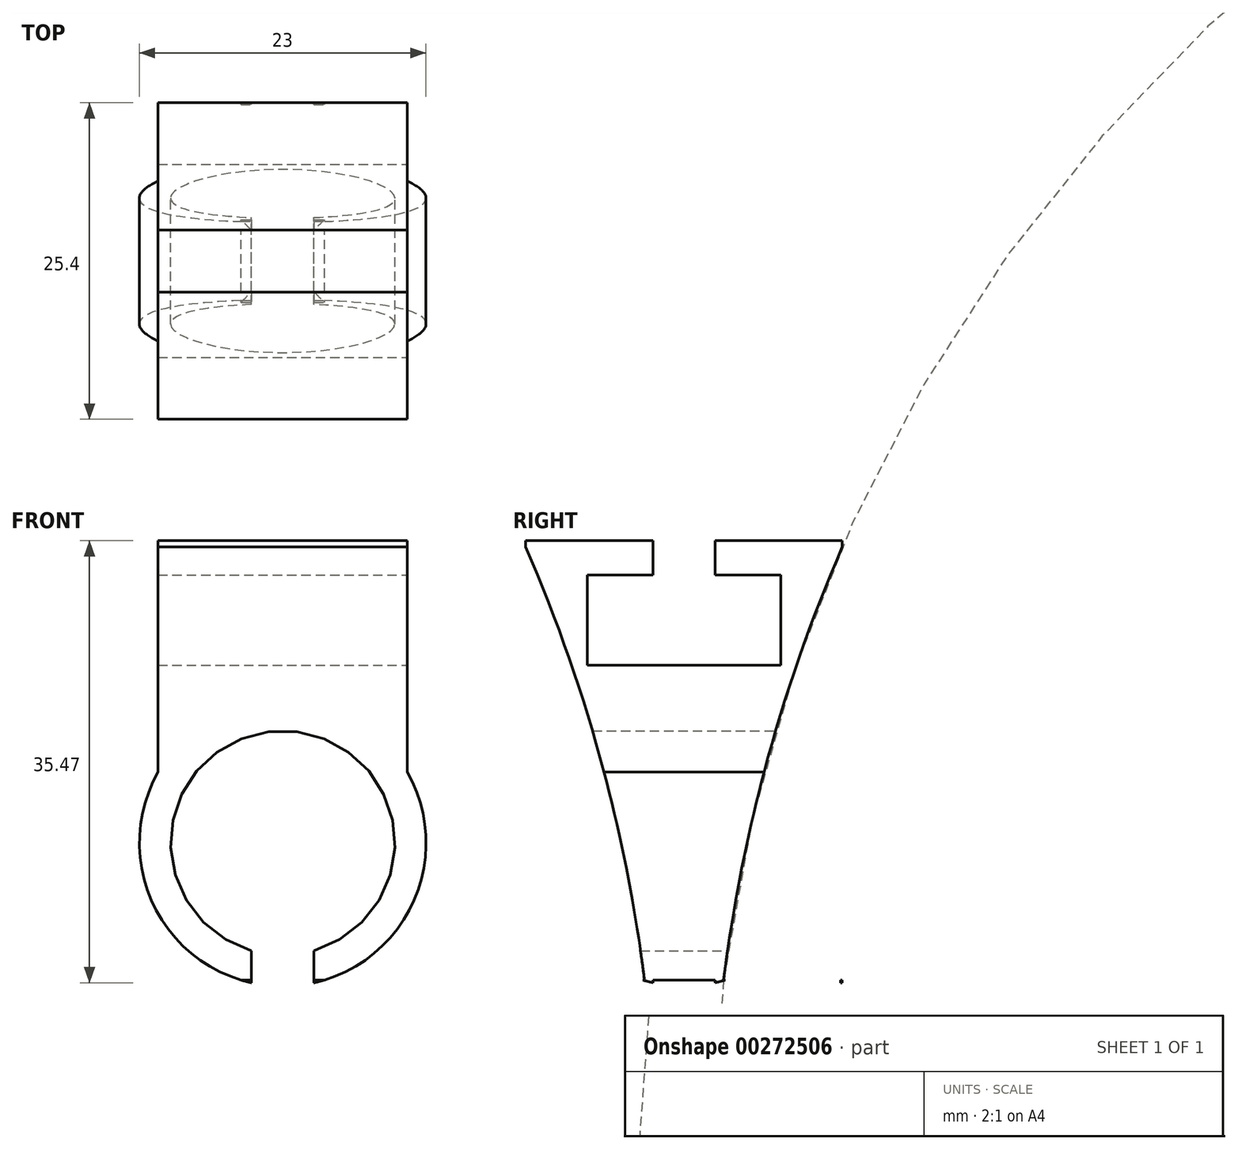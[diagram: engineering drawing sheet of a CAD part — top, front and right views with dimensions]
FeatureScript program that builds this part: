
annotation { "Feature Type Name" : "Feature", "Feature Type Description" : "" }
export const myFeature = defineFeature(function(context is Context, id is Id, definition is map)
    precondition{}
    {
        {
            var Q0;
            Q0=qCreatedBy(makeId("Front.planeOp"),FACE);
            var sketch = newSketch(context, id + "F0", { "sketchPlane" : qUnion([Q0])});
            skArc(sketch, "E0", {"start": v(2.5, -8.65) * mm, "mid": v(0, 9) * mm, "end": v(-2.5, -8.65) * mm});
            skArc(sketch, "E1", {"start": v(2.5, -11.22) * mm, "mid": v(0, 11.5) * mm, "end": v(-2.5, -11.22) * mm});
            skLineSegment(sketch, "E2.left", {"start": v(-2.5, -11.22) * mm, "end": v(-2.5, -8.65) * mm});
            skLineSegment(sketch, "E2.right", {"start": v(2.5, -11.22) * mm, "end": v(2.5, -8.65) * mm});
            skLineSegment(sketch, "E3.bottom", {"start": v(-10, 24.25) * mm, "end": v(-2.5, 24.25) * mm});
            skLineSegment(sketch, "E3.left", {"start": v(-10, 24.25) * mm, "end": v(-10, 11.5) * mm});
            skLineSegment(sketch, "E3.right", {"start": v(10, 24.25) * mm, "end": v(10, 11.5) * mm});
            skLineSegment(sketch, "E4", {"start": v(-2.5, 24.25) * mm, "end": v(-10, 24.25) * mm});
            skLineSegment(sketch, "E5", {"start": v(10, 24.25) * mm, "end": v(2.5, 24.25) * mm});
            skLineSegment(sketch, "E6", {"start": v(2.5, 24.25) * mm, "end": v(10, 24.25) * mm});
            skPoint(sketch, "E7", {"position": v(0, 11.5) * mm});
            skLineSegment(sketch, "E8", {"start": v(-10, 11.5) * mm, "end": v(-10, 5.68) * mm});
            skLineSegment(sketch, "E9", {"start": v(10, 11.5) * mm, "end": v(10, 5.68) * mm});
            skPoint(sketch, "E10.orphan", {"position": v(2.5, 11.5) * mm});
            skPoint(sketch, "E11.end.orphan", {"position": v(-2.5, 11.5) * mm});
            skLineSegment(sketch, "E12", {"start": v(10, 24.25) * mm, "end": v(-10, 24.25) * mm});
            skSolve(sketch);
        }
        {
            var Q0;
            Q0 = qSketchRegion(id + "F0", true);
            extrude(context, id + "F1", {"entities" : qUnion([Q0]), "endBound" : BoundingType.SYMMETRIC, "depth" : 25.4 * mm, "offsetDistance" : 25.4 * mm});
        }
        {
            var Q0;
            Q0=qCreatedBy(makeId("Right.planeOp"),FACE);
            var sketch = newSketch(context, id + "F2", { "sketchPlane" : qUnion([Q0])});
            skLineSegment(sketch, "E13.bottom", {"start": v(12.7, 11) * mm, "end": v(-12.7, 11) * mm});
            skLineSegment(sketch, "E13.top", {"start": v(12.7, -11) * mm, "end": v(-12.7, -11) * mm});
            skLineSegment(sketch, "E13.left", {"start": v(12.7, 11) * mm, "end": v(12.7, -11) * mm});
            skLineSegment(sketch, "E13.right", {"start": v(-12.7, 11) * mm, "end": v(-12.7, -11) * mm});
            skPoint(sketch, "E13.middle", {"position": v(0, 0) * mm});
            skLineSegment(sketch, "E14.bottom", {"start": v(-12.7, -11) * mm, "end": v(12.7, -11) * mm});
            skLineSegment(sketch, "E14.top", {"start": v(-12.7, 23.75) * mm, "end": v(12.7, 23.75) * mm});
            skLineSegment(sketch, "E14.left", {"start": v(-12.7, -11) * mm, "end": v(-12.7, 23.75) * mm});
            skLineSegment(sketch, "E14.right", {"start": v(12.7, -11) * mm, "end": v(12.7, 23.75) * mm});
            skLineSegment(sketch, "E15", {"start": v(0, 0) * mm, "end": v(0, -11) * mm});
            skLineSegment(sketch, "E16", {"start": v(0, -11) * mm, "end": v(3.18, -11) * mm});
            skLineSegment(sketch, "E17", {"start": v(3.18, -11) * mm, "end": v(-3.18, -11) * mm});
            skLineSegment(sketch, "E18", {"start": v(-3.18, -11) * mm, "end": v(3.18, -11) * mm});
            skArc(sketch, "E19", {"start": v(-3.18, -11) * mm, "mid": v(-6.7, 6.71) * mm, "end": v(-12.7, 23.75) * mm});
            skArc(sketch, "E20", {"start": v(12.7, 23.75) * mm, "mid": v(6.7, 6.71) * mm, "end": v(3.17, -11) * mm});
            skLineSegment(sketch, "E21.bottom", {"start": v(-12.7, -11) * mm, "end": v(12.57, -11) * mm});
            skLineSegment(sketch, "E21.top", {"start": v(-12.7, -24.25) * mm, "end": v(12.57, -24.25) * mm});
            skLineSegment(sketch, "E21.left", {"start": v(-12.7, -11) * mm, "end": v(-12.7, -24.25) * mm});
            skLineSegment(sketch, "E21.right", {"start": v(12.57, -11) * mm, "end": v(12.57, -24.25) * mm});
            skArc(sketch, "E22", {"start": v(2.5, -8.64) * mm, "mid": v(0, 9) * mm, "end": v(-2.5, -8.64) * mm});
            skArc(sketch, "E23", {"start": v(2.5, -11.22) * mm, "mid": v(0, 11.5) * mm, "end": v(-2.5, -11.22) * mm});
            skLineSegment(sketch, "E24.left", {"start": v(-2.5, -11.22) * mm, "end": v(-2.5, -8.64) * mm});
            skLineSegment(sketch, "E24.right", {"start": v(2.5, -11.22) * mm, "end": v(2.5, -8.64) * mm});
            skLineSegment(sketch, "E25.bottom", {"start": v(-7.75, 21.5) * mm, "end": v(-2.5, 21.5) * mm});
            skLineSegment(sketch, "E25.top", {"start": v(-7.75, 14.26) * mm, "end": v(7.75, 14.26) * mm});
            skLineSegment(sketch, "E25.left", {"start": v(-7.75, 21.5) * mm, "end": v(-7.75, 14.26) * mm});
            skLineSegment(sketch, "E25.right", {"start": v(7.75, 21.5) * mm, "end": v(7.75, 14.26) * mm});
            skLineSegment(sketch, "E26.bottom", {"start": v(-10, 24.26) * mm, "end": v(-2.5, 24.26) * mm});
            skLineSegment(sketch, "E26.left", {"start": v(-10, 24.26) * mm, "end": v(-10, 11.5) * mm});
            skLineSegment(sketch, "E26.right", {"start": v(10, 24.26) * mm, "end": v(10, 11.5) * mm});
            skLineSegment(sketch, "E27", {"start": v(-2.5, 24.26) * mm, "end": v(-10, 24.26) * mm});
            skLineSegment(sketch, "E28", {"start": v(10, 24.26) * mm, "end": v(2.5, 24.26) * mm});
            skLineSegment(sketch, "E29", {"start": v(2.5, 24.26) * mm, "end": v(10, 24.26) * mm});
            skLineSegment(sketch, "E30", {"start": v(-2.5, 24.26) * mm, "end": v(-2.5, 21.5) * mm});
            skLineSegment(sketch, "E31", {"start": v(-2.5, 21.5) * mm, "end": v(-2.5, 24.26) * mm});
            skLineSegment(sketch, "E32", {"start": v(2.5, 24.26) * mm, "end": v(2.5, 21.5) * mm});
            skPoint(sketch, "E33", {"position": v(0, 11.5) * mm});
            skLineSegment(sketch, "E34", {"start": v(-10, 11.5) * mm, "end": v(-10, 5.69) * mm});
            skLineSegment(sketch, "E35", {"start": v(10, 11.5) * mm, "end": v(10, 5.69) * mm});
            skLineSegment(sketch, "E36.trimOffspring", {"start": v(2.5, 21.5) * mm, "end": v(7.75, 21.5) * mm});
            skPoint(sketch, "E37.orphan", {"position": v(2.5, 11.5) * mm});
            skPoint(sketch, "E38.end.orphan", {"position": v(-2.5, 11.5) * mm});
            skLineSegment(sketch, "E39", {"start": v(2.5, 24.26) * mm, "end": v(-2.5, 24.26) * mm});
            skSolve(sketch);
        }
        {
            var Q0;
            {var subQ7=sQuery(id+"F2.wireOp",EDGE,"E14.left");Q0=makeQuery(id+"F2.imprint","IMPRINT",FACE,{"disambiguationData":[TD([[makeQuery(id+"F2.imprint","IMPRINT",EDGE,{"derivedFrom":subQ7}),-1.0]])]});}
            var Q1;
            {var subQ5=sQuery(id+"F2.wireOp",EDGE,"E39");Q1=makeQuery(id+"F2.imprint","IMPRINT",FACE,{"disambiguationData":[TD([[makeQuery(id+"F2.imprint","IMPRINT",EDGE,{"derivedFrom":subQ5}),1.0]])]});}
            var Q2;
            {var subQ5=sQuery(id+"F2.wireOp",EDGE,"E14.right");Q2=makeQuery(id+"F2.imprint","IMPRINT",FACE,{"disambiguationData":[TD([[makeQuery(id+"F2.imprint","IMPRINT",EDGE,{"derivedFrom":subQ5}),1.0]])]});}
            var Q3;
            {var subQ0=sQuery(id+"F2.wireOp",EDGE,"E35");var subQ1=sQuery(id+"F2.wireOp",EDGE,"E13.bottom");var subQ2=makeQuery(id+"F2.imprint","INTERSECT",VERTEX,{"derivedFrom":[subQ1,subQ0]});Q3=makeQuery(id+"F2.imprint","IMPRINT",FACE,{"disambiguationData":[TD([[makeQuery(id+"F2.imprint","IMPRINT",EDGE,{"disambiguationData":[TD([[subQ2,-1.0]])],"derivedFrom":subQ1}),-1.0]])]});}
            var Q4;
            {var subQ0=sQuery(id+"F2.wireOp",EDGE,"E34");var subQ1=sQuery(id+"F2.wireOp",EDGE,"E13.bottom");var subQ2=makeQuery(id+"F2.imprint","INTERSECT",VERTEX,{"derivedFrom":[subQ1,subQ0]});Q4=makeQuery(id+"F2.imprint","IMPRINT",FACE,{"disambiguationData":[TD([[makeQuery(id+"F2.imprint","IMPRINT",EDGE,{"disambiguationData":[TD([[subQ2,1.0]])],"derivedFrom":subQ1}),-1.0]])]});}
            var Q5;
            {var subQ0=sQuery(id+"F2.wireOp",EDGE,"E34");var subQ1=sQuery(id+"F2.wireOp",EDGE,"E13.bottom");var subQ2=makeQuery(id+"F2.imprint","INTERSECT",VERTEX,{"derivedFrom":[subQ1,subQ0]});Q5=makeQuery(id+"F2.imprint","IMPRINT",FACE,{"disambiguationData":[TD([[makeQuery(id+"F2.imprint","IMPRINT",EDGE,{"disambiguationData":[TD([[subQ2,1.0]])],"derivedFrom":subQ1}),1.0]])]});}
            var Q6;
            {var subQ7=sQuery(id+"F2.wireOp",EDGE,"E13.right");Q6=makeQuery(id+"F2.imprint","IMPRINT",FACE,{"disambiguationData":[TD([[makeQuery(id+"F2.imprint","IMPRINT",EDGE,{"derivedFrom":subQ7}),1.0]])]});}
            var Q7;
            {var subQ0=sQuery(id+"F2.wireOp",EDGE,"E35");var subQ1=sQuery(id+"F2.wireOp",EDGE,"E13.bottom");var subQ2=makeQuery(id+"F2.imprint","INTERSECT",VERTEX,{"derivedFrom":[subQ1,subQ0]});Q7=makeQuery(id+"F2.imprint","IMPRINT",FACE,{"disambiguationData":[TD([[makeQuery(id+"F2.imprint","IMPRINT",EDGE,{"disambiguationData":[TD([[subQ2,-1.0]])],"derivedFrom":subQ1}),1.0]])]});}
            var Q8;
            {var subQ0=sQuery(id+"F2.wireOp",EDGE,"E13.left");Q8=makeQuery(id+"F2.imprint","IMPRINT",FACE,{"disambiguationData":[TD([[makeQuery(id+"F2.imprint","IMPRINT",EDGE,{"derivedFrom":subQ0}),-1.0]])]});}
            var Q9;
            {var subQ1=sQuery(id+"F2.wireOp",EDGE,"E20");var subQ4=sQuery(id+"F2.wireOp",EDGE,"E13.top");var subQ5=makeQuery(id+"F2.imprint","INTERSECT",VERTEX,{"derivedFrom":[subQ4,subQ1]});Q9=makeQuery(id+"F2.imprint","IMPRINT",FACE,{"disambiguationData":[TD([[makeQuery(id+"F2.imprint","IMPRINT",EDGE,{"disambiguationData":[TD([[subQ5,1.0]])],"derivedFrom":subQ4}),-1.0]])]});}
            var Q10;
            {var subQ0=sQuery(id+"F2.wireOp",EDGE,"E22");var subQ1=sQuery(id+"F2.wireOp",EDGE,"E20");var subQ2=makeQuery(id+"F2.imprint","INTERSECT",VERTEX,{"disambiguationData":[OD(0.0)],"derivedFrom":[subQ1,subQ0]});Q10=makeQuery(id+"F2.imprint","IMPRINT",FACE,{"disambiguationData":[TD([[makeQuery(id+"F2.imprint","IMPRINT",EDGE,{"disambiguationData":[TD([[subQ2,-1.0]])],"derivedFrom":subQ1}),1.0]])]});}
            var Q11;
            {var subQ0=sQuery(id+"F2.wireOp",EDGE,"E22");var subQ1=sQuery(id+"F2.wireOp",EDGE,"E19");var subQ2=makeQuery(id+"F2.imprint","INTERSECT",VERTEX,{"disambiguationData":[OD(0.0)],"derivedFrom":[subQ1,subQ0]});Q11=makeQuery(id+"F2.imprint","IMPRINT",FACE,{"disambiguationData":[TD([[makeQuery(id+"F2.imprint","IMPRINT",EDGE,{"disambiguationData":[TD([[subQ2,-1.0]])],"derivedFrom":subQ1}),1.0]])]});}
            var Q12;
            {var subQ4=sQuery(id+"F2.wireOp",EDGE,"E23");var subQ6=sQuery(id+"F2.wireOp",EDGE,"E13.top");var subQ8=makeQuery(id+"F2.imprint","INTERSECT",VERTEX,{"disambiguationData":[OD(0.0)],"derivedFrom":[subQ6,subQ4]});Q12=makeQuery(id+"F2.imprint","IMPRINT",FACE,{"disambiguationData":[TD([[makeQuery(id+"F2.imprint","IMPRINT",EDGE,{"disambiguationData":[TD([[subQ8,1.0]])],"derivedFrom":subQ6}),-1.0]])]});}
            var Q13;
            Q13=makeQuery(id+"F2.imprint","IMPRINT",FACE,{"disambiguationData":[TD([[makeQuery(id+"F2.imprint","IMPRINT",EDGE,{"derivedFrom":sQuery(id+"F2.wireOp",EDGE,"E21.top")}),1.0]])]});
            var Q14;
            {var subQ1=sQuery(id+"F2.wireOp",EDGE,"E25.bottom");Q14=makeQuery(id+"F2.imprint","IMPRINT",FACE,{"disambiguationData":[TD([[makeQuery(id+"F2.imprint","IMPRINT",EDGE,{"derivedFrom":subQ1}),-1.0]])]});}
            extrude(context, id + "F3", {"entities" : qUnion([Q0, Q1, Q2, Q3, Q4, Q5, Q6, Q7, Q8, Q9, Q10, Q11, Q12, Q13, Q14]), "operationType" : NewBodyOperationType.REMOVE, "endBound" : BoundingType.SYMMETRIC, "oppositeDirection" : true, "depth" : 25.4 * mm, "offsetDistance" : 25.4 * mm});
        }
    });
